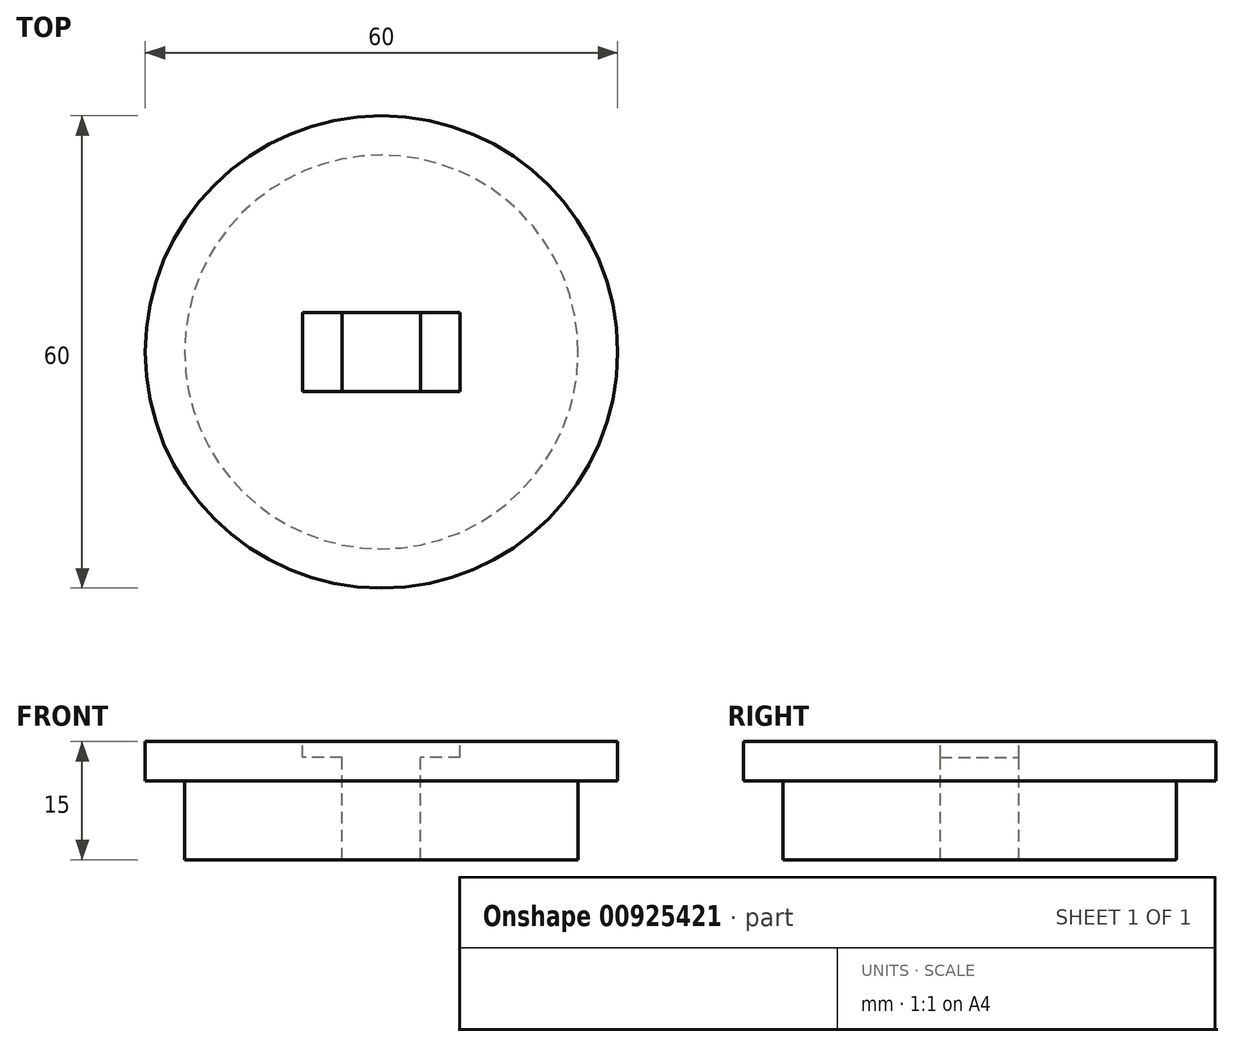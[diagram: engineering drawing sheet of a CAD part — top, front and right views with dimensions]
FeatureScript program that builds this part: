
annotation { "Feature Type Name" : "Feature", "Feature Type Description" : "" }
export const myFeature = defineFeature(function(context is Context, id is Id, definition is map)
    precondition{}
    {
        {
            var Q0;
            Q0=qCreatedBy(makeId("Front.planeOp"),FACE);
            var sketch = newSketch(context, id + "F0", { "sketchPlane" : qUnion([Q0])});
            skLineSegment(sketch, "E0", {"start": v(0, 41.22) * mm, "end": v(0, -46.38) * mm});
            skLineSegment(sketch, "E1", {"start": v(0, 28.62) * mm, "end": v(-30, 28.62) * mm});
            skLineSegment(sketch, "E2", {"start": v(-30, 28.62) * mm, "end": v(-30, 23.62) * mm});
            skLineSegment(sketch, "E3", {"start": v(-30, 23.62) * mm, "end": v(-25, 23.62) * mm});
            skLineSegment(sketch, "E4", {"start": v(-25, 23.62) * mm, "end": v(-25, 13.62) * mm});
            skLineSegment(sketch, "E5", {"start": v(-25, 13.62) * mm, "end": v(0, 13.62) * mm});
            skSolve(sketch);
        }
        {
            var Q0;
            {var subQ0=sQuery(id+"F0.wireOp",EDGE,"E1");Q0=makeQuery(id+"F0.imprint","IMPRINT",FACE,{"disambiguationData":[TD([[makeQuery(id+"F0.imprint","IMPRINT",EDGE,{"derivedFrom":subQ0}),1.0]])]});}
            var Q1;
            Q1=sQuery(id+"F0.wireOp",EDGE,"E0");
            revolve(context, id + "F1", {"surfaceOperationType" : NewSurfaceOperationType.NEW, "entities" : qUnion([Q0]), "axis" : qUnion([Q1]), "revolveType" : RevolveType.FULL});
        }
        {
            var Q0;
            Q0=makeQuery(id+"F1.opRevolve","SWEPT_FACE",FACE,{"disambiguationData":[OSD([sQuery(id+"F0.wireOp",EDGE,"E1")])]});
            var sketch = newSketch(context, id + "F2", { "sketchPlane" : qUnion([Q0])});
            skLineSegment(sketch, "E6.bottom", {"start": v(10, -5) * mm, "end": v(-10, -5) * mm});
            skLineSegment(sketch, "E6.top", {"start": v(10, 5) * mm, "end": v(-10, 5) * mm});
            skLineSegment(sketch, "E6.left", {"start": v(10, -5) * mm, "end": v(10, 5) * mm});
            skLineSegment(sketch, "E6.right", {"start": v(-10, -5) * mm, "end": v(-10, 5) * mm});
            skPoint(sketch, "E6.middle", {"position": v(0, 0) * mm});
            skSolve(sketch);
        }
        {
            var Q0;
            Q0 = qSketchRegion(id + "F2", true);
            extrude(context, id + "F3", {"entities" : qUnion([Q0]), "operationType" : NewBodyOperationType.REMOVE, "oppositeDirection" : true, "depth" : 2 * mm, "offsetDistance" : 25 * mm});
        }
        {
            var Q0;
            Q0=makeQuery(id+"F3.boolean.opBoolean","COPY",FACE,{"derivedFrom":makeQuery(id+"F3.opExtrude","CAP_FACE",FACE,{"disambiguationData":[OSD([sQuery(id+"F2.wireOp",EDGE,"E6.bottom"),sQuery(id+"F2.wireOp",EDGE,"E6.top"),sQuery(id+"F2.wireOp",EDGE,"E6.left"),sQuery(id+"F2.wireOp",EDGE,"E6.right")])],"isStart":false})});
            var sketch = newSketch(context, id + "F4", { "sketchPlane" : qUnion([Q0])});
            skLineSegment(sketch, "E7.bottom", {"start": v(5, -5) * mm, "end": v(-5, -5) * mm});
            skLineSegment(sketch, "E7.top", {"start": v(5, 5) * mm, "end": v(-5, 5) * mm});
            skLineSegment(sketch, "E7.left", {"start": v(5, -5) * mm, "end": v(5, 5) * mm});
            skLineSegment(sketch, "E7.right", {"start": v(-5, -5) * mm, "end": v(-5, 5) * mm});
            skPoint(sketch, "E7.middle", {"position": v(0, 0) * mm});
            skSolve(sketch);
        }
        {
            var Q0;
            Q0 = qSketchRegion(id + "F4", true);
            extrude(context, id + "F5", {"entities" : qUnion([Q0]), "operationType" : NewBodyOperationType.REMOVE, "oppositeDirection" : true, "depth" : 25 * mm, "offsetDistance" : 25 * mm});
        }
    });
